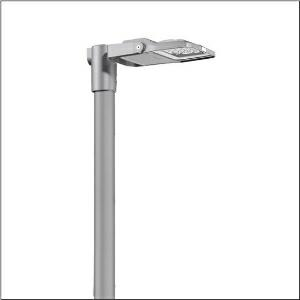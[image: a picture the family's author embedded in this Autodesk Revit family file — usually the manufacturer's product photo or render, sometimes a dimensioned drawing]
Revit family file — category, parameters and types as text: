
# Revit family: floodlight_fl_21_iq_micro___pl33t_5xa7761a4f3a_749b
name_source: partatom
category: Lighting Fixtures
units: mm (PartAtom-declared; Revit-internal decimal feet)

## family parameters
Cut with Voids When Loaded = No
Host = Face
Light Source = No
Part Type = Normal
Room Calculation Point = No
Round Connector Dimension = Use Diameter
Shared = No

## types (1)
- --- (1 x LED, 3050 lm, 23.1 W, 4000K)
    Apparent Load = 23 VA
    CIE Flux Codes = 26 75 99 100 100
    Color Rendering = 70
    Color Temperature = 4000K
    Default Elevation = 1800 mm
    Description = Floodlight FL 21 iQ micro, floodlight, primary light control with lens, of PMMA, primary optical cover: protective disc, of toughened safety glass, transparent, light distribution: PL33T, light emission: direct distribution, installation type: surface-mounted, LED, High Power LED, rated luminous flux: 3.050lm, luminous efficacy: 132lm/W, light colour: 740, colour temperature: 4000K, control gear: iQ Comfort/DALI, control: optimised constant luminous flux control (CLO 2.0), Desk-Remote (wireless, voltage-free reading and setting of iQ features in the workshop via application-optimized NFC function/RFID function), Light-Fading, Smart-Wire, Night-Set, Lumen-Switch, Temp-Guard, Auto-Match, with terminal, 6-pole, mains connection: 220..240V, AC, 50/60Hz, start of lifetime: 23W, end of service life: 24W, reduction: 11W, luminaire housing, of diecast aluminium, powder-coated, Siteco® metallic grey (DB 702S), corrosivity category C5 mid according to DIN EN ISO 12944, suitable for swimming pools, chlorine-resistant, sealing non-destructively replaceable, please order mast flange separately, mast bracket, of steel, galvanised, powder-coated, Siteco® metallic grey (DB 702S), protection rating (complete): IP66, insulation class (complete): insulation class II (safety insulation), certification: CE, ENEC, VDE, protection symbol: D, impact resistance: IK07, permissible operating ambient temperature: -40..+40°C, permissible operating ambient temperature for outdoor applications: -40..+50°C, standard: DIN EN 12944, LABS conformity tested according to VDMA 24364:2018-05, packaging unit: 1 piece

Light Distribution: PL33T
    Height = 65 mm
    Lamp = 1 x LED
    Lamp Light Flux = 3050 lm
    Lamp Power = 23.1 W
    Lamp count = 1
    Length = 312 mm
    Luminous efficacy = 132 lm/W
    Manufacturer = Siteco
    ModVariant = No
    Model = 5XA7761A4F3A
    Number of Poles = 1
    OnlyDefault = Yes
    Power Factor = 1
    Product Name = Floodlight FL 21 iQ micro | PL33T
    Product group = floodlight | pylon annexe
    ProductGroupID = 6200
    Protection Class = Protection class II
    Protection Degree = IP 66
    RLX_Detail_Level = 1
    RLX_Emergency_Light_Flux = 0 lm
    RLX_Emergency_Type = 0
    RLX_Emergency_Type_DB = No
    RlxData = <blob elided: 101949 chars, md5=11d5cc67>
    Socket = socket
    Standby Power = 0 W
    System Light Flux = 3050 lm
    System Power = 23 W
    Type Comments = factory setting: luminous flux: 100 % | dim-lin: 254 | 455 mA
    Type Image = l_1007121.jpg
    URL = http://relux.com
    VarID = @adj_148118
    Voltage = 0 V
    Weight = 0.00 kg
    Width = 230 mm

## geometry (parser evidence)
native form markers: Blend x4, Sweep x12
no freeform markers — native parametric forms only
